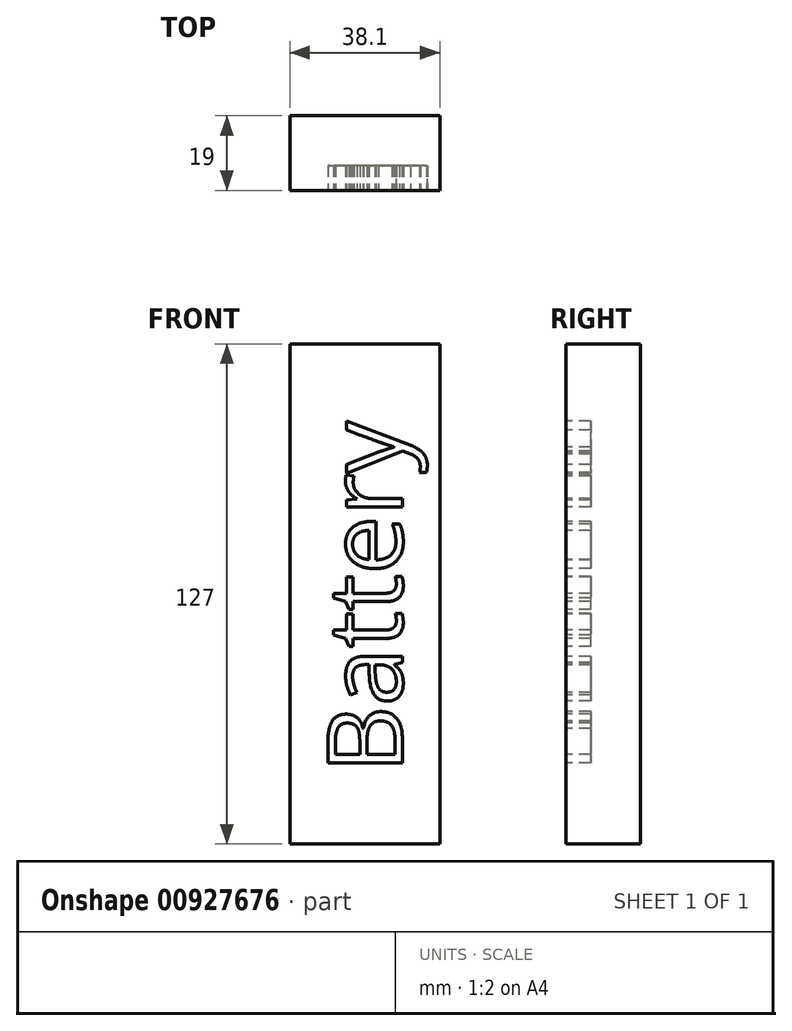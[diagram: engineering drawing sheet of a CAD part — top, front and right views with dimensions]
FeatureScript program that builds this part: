
annotation { "Feature Type Name" : "Feature", "Feature Type Description" : "" }
export const myFeature = defineFeature(function(context is Context, id is Id, definition is map)
    precondition{}
    {
        {
            var Q0;
            Q0=qCreatedBy(makeId("Front.planeOp"),FACE);
            var sketch = newSketch(context, id + "F0", { "sketchPlane" : qUnion([Q0])});
            skLineSegment(sketch, "E0.bottom", {"start": v(-19.05, -63.5) * mm, "end": v(19.05, -63.5) * mm});
            skLineSegment(sketch, "E0.top", {"start": v(-19.05, 63.5) * mm, "end": v(19.05, 63.5) * mm});
            skLineSegment(sketch, "E0.left", {"start": v(-19.05, -63.5) * mm, "end": v(-19.05, 63.5) * mm});
            skLineSegment(sketch, "E0.right", {"start": v(19.05, -63.5) * mm, "end": v(19.05, 63.5) * mm});
            skPoint(sketch, "E0.middle", {"position": v(0, 0) * mm});
            skSolve(sketch);
        }
        {
            var Q0;
            Q0=makeQuery(id+"F0.imprint","IMPRINT",FACE,{"disambiguationData":[TD([[makeQuery(id+"F0.imprint","IMPRINT",EDGE,{"derivedFrom":sQuery(id+"F0.wireOp",EDGE,"E0.bottom")}),1.0]])]});
            extrude(context, id + "F1", {"entities" : qUnion([Q0]), "depth" : 19 * mm, "offsetDistance" : 25.4 * mm});
        }
        {
            var Q0;
            Q0=makeQuery(id+"F1.opExtrude","CAP_FACE",FACE,{"disambiguationData":[OSD([sQuery(id+"F0.wireOp",EDGE,"E0.bottom"),sQuery(id+"F0.wireOp",EDGE,"E0.top"),sQuery(id+"F0.wireOp",EDGE,"E0.left"),sQuery(id+"F0.wireOp",EDGE,"E0.right")])],"isStart":false});
            var sketch = newSketch(context, id + "F2", { "sketchPlane" : qUnion([Q0])});
            skText(sketch, "E1", { "text": "Battery", "fontName": "OpenSans-Regular.ttf"});
            skLineSegment(sketch, "E2", {"start": v(0, 45.6) * mm, "end": v(0, -45.6) * mm, "construction": true});
            const initialGuessF2  = {"E1": [0.00952, -0.0456, 0, 1, 0.01905]};
            skSetInitialGuess(sketch, initialGuessF2);
            skSolve(sketch);
        }
        {
            var Q0;
            Q0 = qSketchRegion(id + "F2", true);
            extrude(context, id + "F3", {"entities" : qUnion([Q0]), "operationType" : NewBodyOperationType.REMOVE, "oppositeDirection" : true, "depth" : 6.35 * mm, "offsetDistance" : 25.4 * mm});
        }
    });
